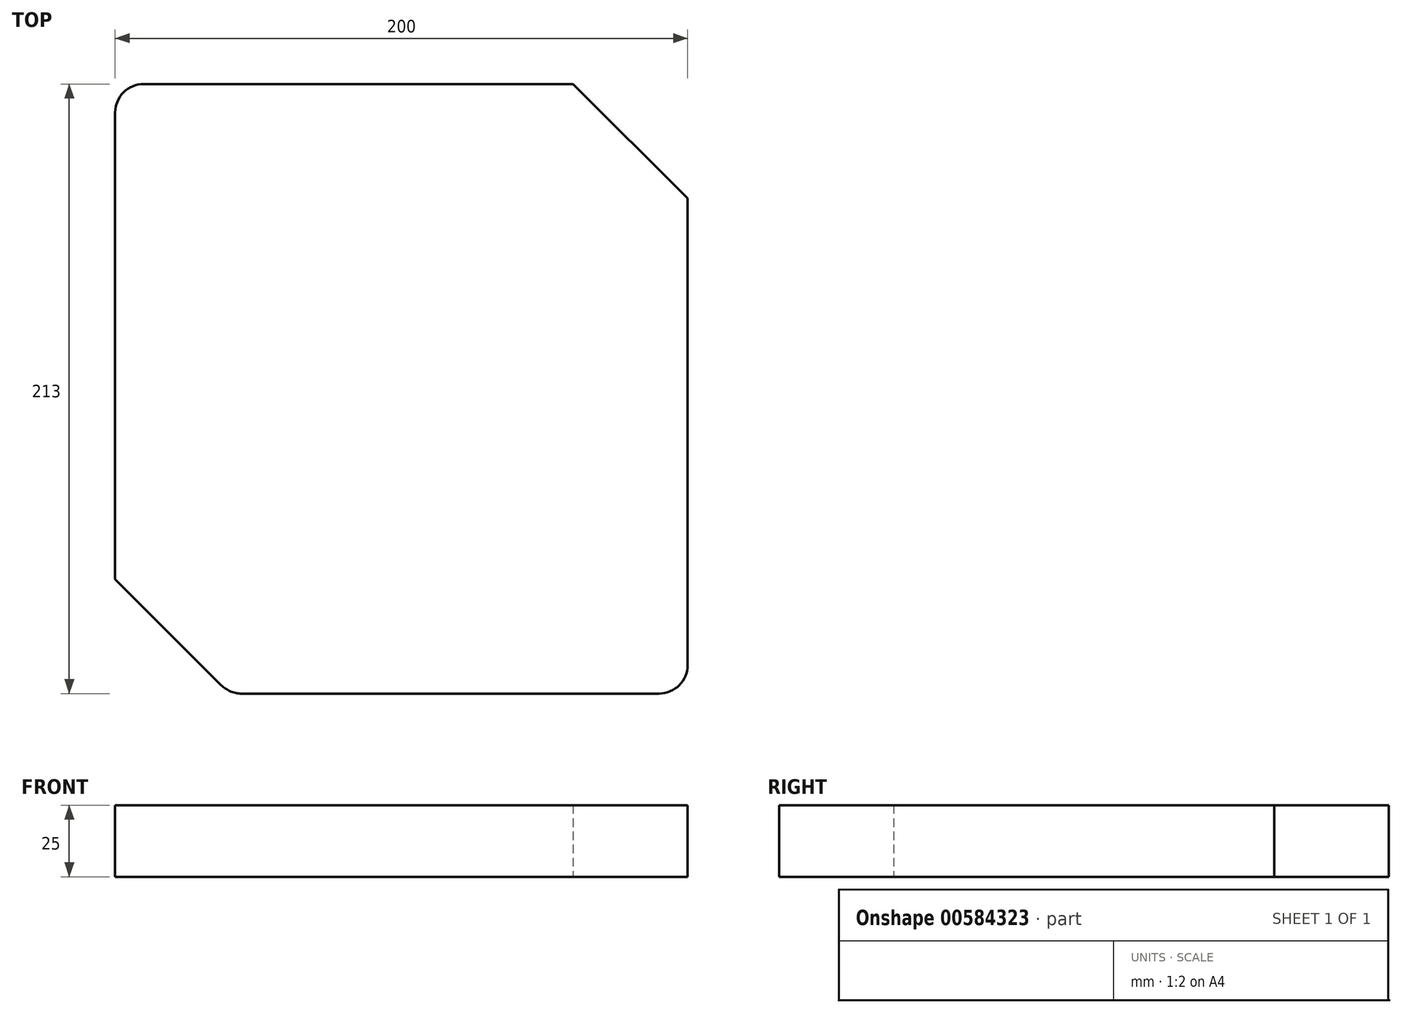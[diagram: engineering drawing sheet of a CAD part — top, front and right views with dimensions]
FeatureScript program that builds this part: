
annotation { "Feature Type Name" : "Feature", "Feature Type Description" : "" }
export const myFeature = defineFeature(function(context is Context, id is Id, definition is map)
    precondition{}
    {
        {
            var Q0;
            Q0=qCreatedBy(makeId("Top.planeOp"),FACE);
            var sketch = newSketch(context, id + "F0", { "sketchPlane" : qUnion([Q0])});
            skLineSegment(sketch, "E0.bottom", {"start": v(60, 106.5) * mm, "end": v(-100, 106.5) * mm});
            skLineSegment(sketch, "E0.top", {"start": v(100, -106.5) * mm, "end": v(-70, -106.5) * mm});
            skLineSegment(sketch, "E0.left", {"start": v(100, 66.5) * mm, "end": v(100, -106.5) * mm});
            skLineSegment(sketch, "E0.right", {"start": v(-100, 106.5) * mm, "end": v(-100, -66.5) * mm});
            skPoint(sketch, "E0.middle", {"position": v(0, 0) * mm});
            skLineSegment(sketch, "E1.bottom", {"start": v(100, -106.5) * mm, "end": v(31, -106.5) * mm});
            skLineSegment(sketch, "E1.top", {"start": v(100, -37.5) * mm, "end": v(31, -37.5) * mm});
            skLineSegment(sketch, "E1.left", {"start": v(100, -106.5) * mm, "end": v(100, -37.5) * mm});
            skLineSegment(sketch, "E1.right", {"start": v(31, -106.5) * mm, "end": v(31, -37.5) * mm});
            skLineSegment(sketch, "E2.bottom", {"start": v(100, -106.5) * mm, "end": v(-46, -106.5) * mm});
            skLineSegment(sketch, "E3.bottom", {"start": v(-70, -106.5) * mm, "end": v(-60, -106.5) * mm});
            skLineSegment(sketch, "E4", {"start": v(-100, -66.5) * mm, "end": v(-60, -106.5) * mm});
            skLineSegment(sketch, "E5", {"start": v(60, 106.5) * mm, "end": v(100, 66.5) * mm});
            skArc(sketch, "E6", {"start": v(-100, -40.1) * mm, "mid": v(-19.12, -25.6) * mm, "end": v(31, 39.5) * mm});
            skPoint(sketch, "E6.first.point", {"position": v(-46, -37.5) * mm});
            skPoint(sketch, "E6.second.point", {"position": v(31, 39.5) * mm});
            skLineSegment(sketch, "E7.top", {"start": v(100, 63.5) * mm, "end": v(-70, 63.5) * mm, "construction": true});
            skLineSegment(sketch, "E7.left", {"start": v(100, -106.5) * mm, "end": v(100, 63.5) * mm});
            skLineSegment(sketch, "E7.right", {"start": v(-70, -106.5) * mm, "end": v(-70, 63.5) * mm, "construction": true});
            skLineSegment(sketch, "E8", {"start": v(31, 39.5) * mm, "end": v(100, 39.5) * mm});
            skLineSegment(sketch, "E9", {"start": v(-46, -37.5) * mm, "end": v(-46, -106.5) * mm});
            skSolve(sketch);
        }
        {
            var Q0;
            {var subQ1=sQuery(id+"F0.wireOp",EDGE,"E0.bottom");Q0=makeQuery(id+"F0.imprint","IMPRINT",FACE,{"disambiguationData":[TD([[makeQuery(id+"F0.imprint","IMPRINT",EDGE,{"derivedFrom":subQ1}),1.0]])]});}
            var Q1;
            {var subQ5=sQuery(id+"F0.wireOp",EDGE,"E1.top");Q1=makeQuery(id+"F0.imprint","IMPRINT",FACE,{"disambiguationData":[TD([[makeQuery(id+"F0.imprint","IMPRINT",EDGE,{"derivedFrom":subQ5}),-1.0]])]});}
            var Q2;
            {var subQ1=sQuery(id+"F0.wireOp",EDGE,"E4");Q2=makeQuery(id+"F0.imprint","IMPRINT",FACE,{"disambiguationData":[TD([[makeQuery(id+"F0.imprint","IMPRINT",EDGE,{"derivedFrom":subQ1}),1.0]])]});}
            var Q3;
            {var subQ0=sQuery(id+"F0.wireOp",EDGE,"E1.top");Q3=makeQuery(id+"F0.imprint","IMPRINT",FACE,{"disambiguationData":[TD([[makeQuery(id+"F0.imprint","IMPRINT",EDGE,{"derivedFrom":subQ0}),1.0]])]});}
            extrude(context, id + "F1", {"entities" : qUnion([Q0, Q1, Q2, Q3]), "depth" : 25 * mm, "offsetDistance" : 25 * mm});
        }
        {
            var Q0;
            Q0=makeQuery(id+"F1.opExtrude","SWEPT_EDGE",EDGE,{"disambiguationData":[OSD([sQuery(id+"F0.wireOp",EDGE,"E0.bottom"),sQuery(id+"F0.wireOp",EDGE,"E0.right")])]});
            fillet(context, id + "F2", {"entities" : qUnion([Q0]), "radius" : 10 * mm, "tangentPropagation" : true, "allowEdgeOverflow" : false});
        }
        {
            var Q0;
            Q0=makeQuery(id+"F1.opExtrude","SWEPT_EDGE",EDGE,{"disambiguationData":[OSD([sQuery(id+"F0.wireOp",EDGE,"E0.top"),sQuery(id+"F0.wireOp",EDGE,"E7.left")])]});
            fillet(context, id + "F3", {"entities" : qUnion([Q0]), "radius" : 10 * mm, "tangentPropagation" : true, "allowEdgeOverflow" : false});
        }
    });
